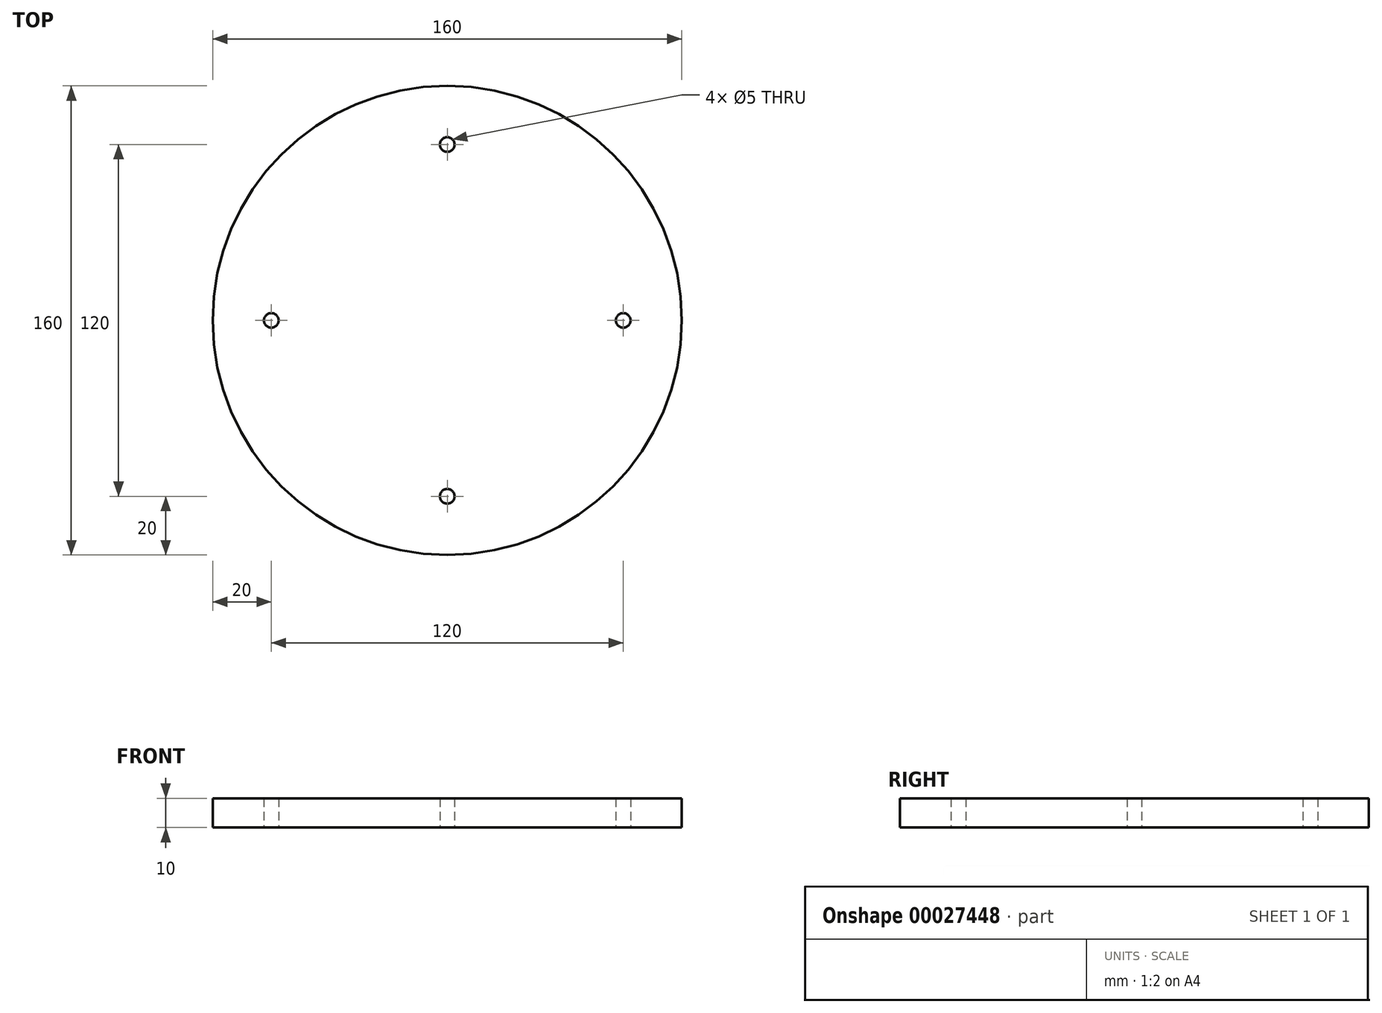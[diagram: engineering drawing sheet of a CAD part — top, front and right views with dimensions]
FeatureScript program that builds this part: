
annotation { "Feature Type Name" : "Feature", "Feature Type Description" : "" }
export const myFeature = defineFeature(function(context is Context, id is Id, definition is map)
    precondition{}
    {
        {
            var Q0;
            Q0=qCreatedBy(makeId("Top.planeOp"),FACE);
            var sketch = newSketch(context, id + "F0", { "sketchPlane" : qUnion([Q0])});
            skCircle(sketch, "E0", {"center": v(0, 0) * mm, "radius": 80 * mm});
            skSolve(sketch);
        }
        {
            var Q0;
            Q0 = qSketchRegion(id + "F0", true);
            extrude(context, id + "F1", {"entities" : qUnion([Q0]), "oppositeDirection" : true, "depth" : 10 * mm});
        }
        {
            var Q0;
            Q0=makeQuery(id+"F1.opExtrude","CAP_FACE",FACE,{"disambiguationData":[OSD([sQuery(id+"F0.wireOp",EDGE,"E0")])],"isStart":false});
            var sketch = newSketch(context, id + "F2", { "sketchPlane" : qUnion([Q0])});
            skCircle(sketch, "E1.0", {"center": v(0, 0) * mm, "radius": 80 * mm});
            skLineSegment(sketch, "E2", {"start": v(0, 80) * mm, "end": v(0, -80) * mm, "construction": true});
            skLineSegment(sketch, "E3", {"start": v(80, 0) * mm, "end": v(-80, 0) * mm, "construction": true});
            skCircle(sketch, "E4", {"center": v(-60, 0) * mm, "radius": 2.5 * mm});
            skCircle(sketch, "E5", {"center": v(0, 60) * mm, "radius": 2.5 * mm});
            skCircle(sketch, "E6", {"center": v(60, 0) * mm, "radius": 2.5 * mm});
            skCircle(sketch, "E7", {"center": v(0, -60) * mm, "radius": 2.5 * mm});
            skSolve(sketch);
        }
        {
            var Q0;
            Q0=makeQuery(id+"F2.imprint","IMPRINT",FACE,{"disambiguationData":[TD([[makeQuery(id+"F2.imprint","IMPRINT",EDGE,{"derivedFrom":sQuery(id+"F2.wireOp",EDGE,"E4")}),1.0]])]});
            var Q1;
            Q1=makeQuery(id+"F2.imprint","IMPRINT",FACE,{"disambiguationData":[TD([[makeQuery(id+"F2.imprint","IMPRINT",EDGE,{"derivedFrom":sQuery(id+"F2.wireOp",EDGE,"E5")}),1.0]])]});
            var Q2;
            Q2=makeQuery(id+"F2.imprint","IMPRINT",FACE,{"disambiguationData":[TD([[makeQuery(id+"F2.imprint","IMPRINT",EDGE,{"derivedFrom":sQuery(id+"F2.wireOp",EDGE,"E6")}),1.0]])]});
            var Q3;
            Q3=makeQuery(id+"F2.imprint","IMPRINT",FACE,{"disambiguationData":[TD([[makeQuery(id+"F2.imprint","IMPRINT",EDGE,{"derivedFrom":sQuery(id+"F2.wireOp",EDGE,"E7")}),1.0]])]});
            extrude(context, id + "F3", {"entities" : qUnion([Q0, Q1, Q2, Q3]), "operationType" : NewBodyOperationType.REMOVE, "oppositeDirection" : true, "depth" : (5 * 2) * mm});
        }
    });
